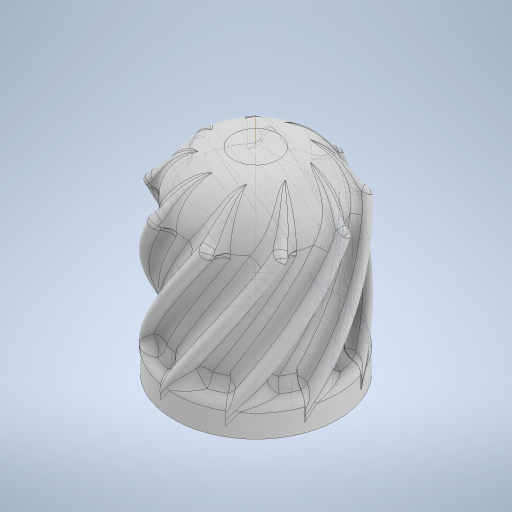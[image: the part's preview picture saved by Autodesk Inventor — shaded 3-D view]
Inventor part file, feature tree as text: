
AUTODESK INVENTOR PART (.ipt)
format: ipt  version: 2023 (Build 270158030, 158C)  size: 2,111,488 bytes
history: native  units: mm
features: fillet x6, sketch x4, projected_geometry x4, extrude x3, helix x1, pattern_circular x1
ambient origin geometry x8: Origin, YZ Plane, XZ Plane, XY Plane, X Axis, Y Axis, Z Axis, Center Point
bodies: Solid1 (feature_tree)
feature tree (19):
  extrude  "Extrusion1"  Depth=16.5mm TaperAngle=0.0deg
  extrude  "Extrusion2"  Depth=7.1mm
  extrude  "Extrusion3"  Depth=3.55mm
  fillet  "Fillet1"  Radius=13.2mm
  helix  "Coil1"  [1 undecoded]
  fillet  "Fillet3"  Radius=13.8mm
  fillet  "Fillet2"  Radius=2.4mm
  pattern_circular  "Circular Pattern1"  [2 undecoded]
  fillet  "Fillet5"  Radius=1.0mm
  fillet  "Fillet6"  Radius=0.1mm
  fillet  "Fillet4"  Radius=90.0mm
  sketch  "Sketch1"  dims[d0=13.85mm d1=16.5mm d2=0.0mm]
  sketch  "Sketch2"  dims[d3=7.1mm d4=7.1mm]
  sketch  "Sketch3"  dims[d5=3.55mm d6=3.55mm d7=13.2mm d8=0.0mm d9=11.6mm d10=13.8mm d11=0.0mm d12=2.4mm]
  projected_geometry  "Projected Loop1"
  sketch  "Sketch4"  dims[d13=1.2mm d14=70.0mm d15=12.0mm d16=2.0mm d17=0.0mm d18=90.0deg d19=90.0deg d20=0.0mm d21=0.174533mm d22=3.9mm d23=0.9mm d24=1.0mm d25=0.1mm d26=90.0mm d27=360.0deg d29=0.5mm d30=0.5mm]
  projected_geometry  "Projected Loop2"
  projected_geometry  "Projected Loop3"
  projected_geometry  "Projected Loop4"
note: 3 required parameter values undecoded (feature->parameter linkage not recoverable at this tier; creation-order binding heuristic only, values carry confidence <= 0.55)
